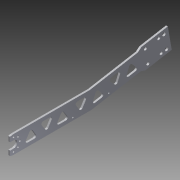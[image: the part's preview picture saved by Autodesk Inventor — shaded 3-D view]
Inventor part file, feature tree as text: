
AUTODESK INVENTOR PART (.ipt)
format: ipt  version: 2013 (Build 170138000, 138)  size: 2,889,728 bytes
history: native  units: mm
features: sketch x8, hole x5, extrude x3, other x2, pattern_circular x1, fillet x1
ambient origin geometry x8: Origin, YZ Plane, XZ Plane, XY Plane, X Axis, Y Axis, Z Axis, Center Point
feature tree (20):
  other  "ソリッド1"
  extrude  "押し出し1"  Depth=20.0mm
  hole  "穴2"  [1 undecoded]
  extrude  "押し出し2"  Depth=10.0mm
  hole  "穴3"  [1 undecoded]
  hole  "穴4"  [1 undecoded]
  pattern_circular  "円形状パターン3"  [2 undecoded]
  hole  "穴5"  [1 undecoded]
  hole  "穴6"  [1 undecoded]
  extrude  "押し出し4"  Depth=4.0mm
  fillet  "フィレット1"  Radius=170.0mm
  sketch  "スケッチ2"
  sketch  "スケッチ4"
  sketch  "スケッチ5"
  sketch  "スケッチ6"
  sketch  "スケッチ7"
  sketch  "スケッチ8"
  sketch  "スケッチ11"
  sketch  "スケッチ13"
  other  "断面エッジを投影1"
note: 7 required parameter values undecoded (feature->parameter linkage not recoverable at this tier; creation-order binding heuristic only, values carry confidence <= 0.55)
